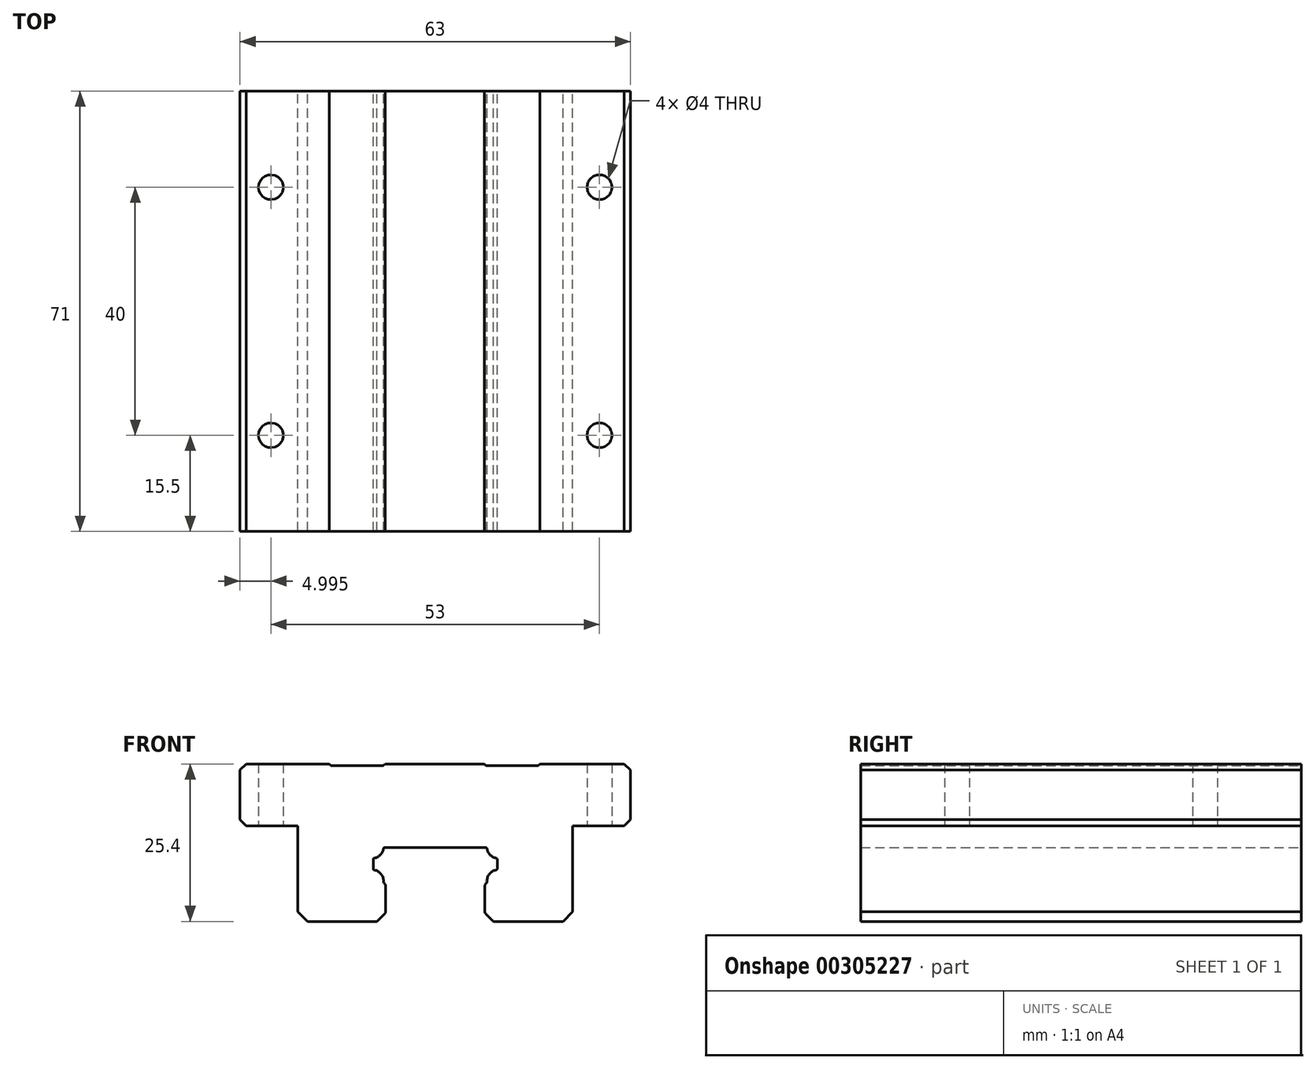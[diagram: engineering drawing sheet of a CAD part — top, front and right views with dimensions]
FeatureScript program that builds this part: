
annotation { "Feature Type Name" : "Feature", "Feature Type Description" : "" }
export const myFeature = defineFeature(function(context is Context, id is Id, definition is map)
    precondition{}
    {
        {
            var Q0;
            Q0=qCreatedBy(makeId("Front.planeOp"),FACE);
            var sketch = newSketch(context, id + "F0", { "sketchPlane" : qUnion([Q0])});
            skLineSegment(sketch, "E0.0.0", {"start": v(9.4, -11.6) * mm, "end": v(9.42, -11.62) * mm});
            skLineSegment(sketch, "E0.0.1", {"start": v(9.42, -11.62) * mm, "end": v(20.62, -11.62) * mm});
            skLineSegment(sketch, "E0.0.2", {"start": v(20.62, -11.62) * mm, "end": v(22.17, -10.07) * mm});
            skLineSegment(sketch, "E0.0.3", {"start": v(22.17, -10.07) * mm, "end": v(22.17, -7.4) * mm});
            skLineSegment(sketch, "E0.0.7", {"start": v(30.04, 3.78) * mm, "end": v(30.52, 3.78) * mm});
            skLineSegment(sketch, "E0.0.8", {"start": v(30.52, 3.78) * mm, "end": v(31.52, 4.78) * mm});
            skLineSegment(sketch, "E0.0.9", {"start": v(31.52, 4.78) * mm, "end": v(31.52, 12.78) * mm});
            skLineSegment(sketch, "E0.0.10", {"start": v(31.52, 12.78) * mm, "end": v(30.52, 13.78) * mm});
            skLineSegment(sketch, "E0.0.11", {"start": v(30.52, 13.78) * mm, "end": v(16.92, 13.78) * mm});
            skLineSegment(sketch, "E0.0.12", {"start": v(16.92, 13.78) * mm, "end": v(16.76, 13.63) * mm});
            skArc(sketch, "E0.0.13", {"start": v(16.76, 13.63) * mm, "mid": v(16.6, 13.52) * mm, "end": v(16.4, 13.48) * mm});
            skLineSegment(sketch, "E0.0.14", {"start": v(16.4, 13.48) * mm, "end": v(8.42, 13.48) * mm});
            skArc(sketch, "E0.0.15", {"start": v(8.42, 13.48) * mm, "mid": v(8.23, 13.52) * mm, "end": v(8.07, 13.63) * mm});
            skLineSegment(sketch, "E0.0.16", {"start": v(8.07, 13.63) * mm, "end": v(7.92, 13.78) * mm});
            skLineSegment(sketch, "E0.0.17", {"start": v(7.92, 13.78) * mm, "end": v(-8.08, 13.78) * mm});
            skLineSegment(sketch, "E0.0.18", {"start": v(-8.08, 13.78) * mm, "end": v(-8.24, 13.63) * mm});
            skArc(sketch, "E0.0.19", {"start": v(-8.24, 13.63) * mm, "mid": v(-8.4, 13.52) * mm, "end": v(-8.6, 13.48) * mm});
            skLineSegment(sketch, "E0.0.20", {"start": v(-8.6, 13.48) * mm, "end": v(-16.58, 13.48) * mm});
            skArc(sketch, "E0.0.21", {"start": v(-16.58, 13.48) * mm, "mid": v(-16.77, 13.52) * mm, "end": v(-16.93, 13.63) * mm});
            skLineSegment(sketch, "E0.0.22", {"start": v(-16.93, 13.63) * mm, "end": v(-17.08, 13.78) * mm});
            skLineSegment(sketch, "E0.0.23", {"start": v(-17.08, 13.78) * mm, "end": v(-30.48, 13.78) * mm});
            skLineSegment(sketch, "E0.0.24", {"start": v(-30.48, 13.78) * mm, "end": v(-31.48, 12.78) * mm});
            skLineSegment(sketch, "E0.0.25", {"start": v(-31.48, 12.78) * mm, "end": v(-31.48, 4.78) * mm});
            skLineSegment(sketch, "E0.0.26", {"start": v(-31.48, 4.78) * mm, "end": v(-30.48, 3.78) * mm});
            skLineSegment(sketch, "E0.0.27", {"start": v(-30.48, 3.78) * mm, "end": v(-30, 3.78) * mm});
            skLineSegment(sketch, "E0.0.31", {"start": v(-22.13, -7.4) * mm, "end": v(-22.13, -10.07) * mm});
            skLineSegment(sketch, "E0.0.32", {"start": v(-22.13, -10.07) * mm, "end": v(-20.58, -11.62) * mm});
            skLineSegment(sketch, "E0.0.33", {"start": v(-20.58, -11.62) * mm, "end": v(-9.38, -11.62) * mm});
            skLineSegment(sketch, "E0.0.34", {"start": v(-9.38, -11.62) * mm, "end": v(-9.37, -11.6) * mm});
            skLineSegment(sketch, "E0.0.35", {"start": v(-9.37, -11.6) * mm, "end": v(-19.73, -11.6) * mm});
            skLineSegment(sketch, "E0.0.43", {"start": v(19.77, -11.6) * mm, "end": v(9.4, -11.6) * mm});
            skLineSegment(sketch, "E1.0.0", {"start": v(8.16, -10.36) * mm, "end": v(9.4, -11.6) * mm});
            skLineSegment(sketch, "E1.0.1", {"start": v(9.4, -11.6) * mm, "end": v(19.77, -11.6) * mm});
            skLineSegment(sketch, "E1.0.9", {"start": v(-19.73, -11.6) * mm, "end": v(-9.37, -11.6) * mm});
            skLineSegment(sketch, "E1.0.10", {"start": v(-9.37, -11.6) * mm, "end": v(-8.13, -10.36) * mm});
            skArc(sketch, "E1.0.11", {"start": v(-8.13, -10.36) * mm, "mid": v(-8.02, -10.2) * mm, "end": v(-7.98, -10.01) * mm});
            skLineSegment(sketch, "E1.0.12", {"start": v(-7.98, -10.01) * mm, "end": v(-7.98, -5.93) * mm});
            skArc(sketch, "E1.0.13", {"start": v(-7.98, -5.93) * mm, "mid": v(-8.02, -5.73) * mm, "end": v(-8.13, -5.57) * mm});
            skLineSegment(sketch, "E1.0.14", {"start": v(-8.13, -5.57) * mm, "end": v(-8.27, -5.43) * mm});
            skArc(sketch, "E1.0.15", {"start": v(-8.27, -5.43) * mm, "mid": v(-8.32, -5.36) * mm, "end": v(-8.33, -5.27) * mm});
            skArc(sketch, "E1.0.16", {"start": v(-8.33, -5.27) * mm, "mid": v(-8.7, -4) * mm, "end": v(-9.82, -3.33) * mm});
            skArc(sketch, "E1.0.17", {"start": v(-9.82, -3.33) * mm, "mid": v(-9.94, -3.26) * mm, "end": v(-9.98, -3.13) * mm});
            skLineSegment(sketch, "E1.0.18", {"start": v(-9.98, -3.13) * mm, "end": v(-9.98, -1.6) * mm});
            skArc(sketch, "E1.0.19", {"start": v(-9.98, -1.6) * mm, "mid": v(-9.94, -1.47) * mm, "end": v(-9.82, -1.4) * mm});
            skArc(sketch, "E1.0.20", {"start": v(-9.82, -1.4) * mm, "mid": v(-8.83, -0.89) * mm, "end": v(-8.34, 0.11) * mm});
            skArc(sketch, "E1.0.21", {"start": v(-8.34, 0.11) * mm, "mid": v(-8.27, 0.23) * mm, "end": v(-8.14, 0.28) * mm});
            skLineSegment(sketch, "E1.0.22", {"start": v(-8.14, 0.28) * mm, "end": v(8.17, 0.28) * mm});
            skArc(sketch, "E1.0.23", {"start": v(8.17, 0.28) * mm, "mid": v(8.3, 0.23) * mm, "end": v(8.37, 0.11) * mm});
            skArc(sketch, "E1.0.24", {"start": v(8.37, 0.11) * mm, "mid": v(8.86, -0.89) * mm, "end": v(9.85, -1.4) * mm});
            skArc(sketch, "E1.0.25", {"start": v(9.85, -1.4) * mm, "mid": v(9.97, -1.47) * mm, "end": v(10.02, -1.6) * mm});
            skLineSegment(sketch, "E1.0.26", {"start": v(10.02, -1.6) * mm, "end": v(10.02, -3.13) * mm});
            skArc(sketch, "E1.0.27", {"start": v(10.02, -3.13) * mm, "mid": v(9.97, -3.26) * mm, "end": v(9.85, -3.33) * mm});
            skArc(sketch, "E1.0.28", {"start": v(9.85, -3.33) * mm, "mid": v(8.72, -4) * mm, "end": v(8.36, -5.27) * mm});
            skArc(sketch, "E1.0.29", {"start": v(8.36, -5.27) * mm, "mid": v(8.35, -5.36) * mm, "end": v(8.3, -5.43) * mm});
            skLineSegment(sketch, "E1.0.30", {"start": v(8.3, -5.43) * mm, "end": v(8.16, -5.57) * mm});
            skArc(sketch, "E1.0.31", {"start": v(8.16, -5.57) * mm, "mid": v(8.05, -5.73) * mm, "end": v(8.02, -5.93) * mm});
            skLineSegment(sketch, "E1.0.32", {"start": v(8.02, -5.93) * mm, "end": v(8.02, -10.01) * mm});
            skArc(sketch, "E1.0.33", {"start": v(8.02, -10.01) * mm, "mid": v(8.05, -10.2) * mm, "end": v(8.16, -10.36) * mm});
            skLineSegment(sketch, "E2", {"start": v(-30.48, 3.78) * mm, "end": v(-22.13, 3.78) * mm});
            skLineSegment(sketch, "E3", {"start": v(-22.13, 3.78) * mm, "end": v(-22.13, -7.4) * mm});
            skLineSegment(sketch, "E4", {"start": v(22.17, -7.4) * mm, "end": v(22.17, 3.78) * mm});
            skLineSegment(sketch, "E5", {"start": v(22.17, 3.78) * mm, "end": v(30.04, 3.78) * mm});
            skSolve(sketch);
        }
        {
            var Q0;
            Q0=makeQuery(id+"F0.imprint","IMPRINT",FACE,{"disambiguationData":[TD([[makeQuery(id+"F0.imprint","IMPRINT",EDGE,{"derivedFrom":sQuery(id+"F0.wireOp",EDGE,"E0.0.0")}),1.0]])]});
            extrude(context, id + "F1", {"entities" : qUnion([Q0]), "depth" : 71 * mm});
        }
        {
            var Q0;
            Q0=makeQuery(id+"F1.opExtrude","SWEPT_FACE",FACE,{"disambiguationData":[OSD([sQuery(id+"F0.wireOp",EDGE,"E1.0.22")])]});
            var sketch = newSketch(context, id + "F2", { "sketchPlane" : qUnion([Q0])});
            skLineSegment(sketch, "E6.0", {"start": v(-31.48, 71) * mm, "end": v(-31.48, 0) * mm});
            skLineSegment(sketch, "E7.0", {"start": v(31.52, 71) * mm, "end": v(31.52, 0) * mm});
            skLineSegment(sketch, "E8.0", {"start": v(0.02, 71) * mm, "end": v(0.02, 0) * mm});
            skPoint(sketch, "E9", {"position": v(-26.48, 55.5) * mm});
            skPoint(sketch, "E10", {"position": v(26.52, 55.5) * mm});
            skPoint(sketch, "E11", {"position": v(-26.48, 15.5) * mm});
            skPoint(sketch, "E12", {"position": v(26.52, 15.5) * mm});
            skSolve(sketch);
        }
        {
            var Q0;
            Q0=sQuery(id+"F2.wireOp",VERTEX,"E9");
            var Q1;
            Q1=sQuery(id+"F2.wireOp",VERTEX,"E10");
            var Q2;
            Q2=sQuery(id+"F2.wireOp",VERTEX,"E12");
            var Q3;
            Q3=sQuery(id+"F2.wireOp",VERTEX,"E11");
            var Q4;
            Q4=makeQuery(id+"F1.opExtrude","SWEPT_BODY",BODY,{"disambiguationData":[OSD([sQuery(id+"F0.wireOp",EDGE,"E0.0.0"),sQuery(id+"F0.wireOp",EDGE,"E0.0.1"),sQuery(id+"F0.wireOp",EDGE,"E0.0.2"),sQuery(id+"F0.wireOp",EDGE,"E0.0.3"),sQuery(id+"F0.wireOp",EDGE,"E0.0.7"),sQuery(id+"F0.wireOp",EDGE,"E0.0.8"),sQuery(id+"F0.wireOp",EDGE,"E0.0.9"),sQuery(id+"F0.wireOp",EDGE,"E0.0.10"),sQuery(id+"F0.wireOp",EDGE,"E0.0.11"),sQuery(id+"F0.wireOp",EDGE,"E0.0.12"),sQuery(id+"F0.wireOp",EDGE,"E0.0.13"),sQuery(id+"F0.wireOp",EDGE,"E0.0.14"),sQuery(id+"F0.wireOp",EDGE,"E0.0.15"),sQuery(id+"F0.wireOp",EDGE,"E0.0.16"),sQuery(id+"F0.wireOp",EDGE,"E0.0.17"),sQuery(id+"F0.wireOp",EDGE,"E0.0.18"),sQuery(id+"F0.wireOp",EDGE,"E0.0.19"),sQuery(id+"F0.wireOp",EDGE,"E0.0.20"),sQuery(id+"F0.wireOp",EDGE,"E0.0.21"),sQuery(id+"F0.wireOp",EDGE,"E0.0.22"),sQuery(id+"F0.wireOp",EDGE,"E0.0.23"),sQuery(id+"F0.wireOp",EDGE,"E0.0.24"),sQuery(id+"F0.wireOp",EDGE,"E0.0.25"),sQuery(id+"F0.wireOp",EDGE,"E0.0.26"),sQuery(id+"F0.wireOp",EDGE,"E0.0.31"),sQuery(id+"F0.wireOp",EDGE,"E0.0.32"),sQuery(id+"F0.wireOp",EDGE,"E0.0.33"),sQuery(id+"F0.wireOp",EDGE,"E0.0.34"),sQuery(id+"F0.wireOp",EDGE,"E1.0.0"),sQuery(id+"F0.wireOp",EDGE,"E1.0.10"),sQuery(id+"F0.wireOp",EDGE,"E1.0.11"),sQuery(id+"F0.wireOp",EDGE,"E1.0.12"),sQuery(id+"F0.wireOp",EDGE,"E1.0.13"),sQuery(id+"F0.wireOp",EDGE,"E1.0.14"),sQuery(id+"F0.wireOp",EDGE,"E1.0.15"),sQuery(id+"F0.wireOp",EDGE,"E1.0.16"),sQuery(id+"F0.wireOp",EDGE,"E1.0.17"),sQuery(id+"F0.wireOp",EDGE,"E1.0.18"),sQuery(id+"F0.wireOp",EDGE,"E1.0.19"),sQuery(id+"F0.wireOp",EDGE,"E1.0.20"),sQuery(id+"F0.wireOp",EDGE,"E1.0.21"),sQuery(id+"F0.wireOp",EDGE,"E1.0.22"),sQuery(id+"F0.wireOp",EDGE,"E1.0.23"),sQuery(id+"F0.wireOp",EDGE,"E1.0.24"),sQuery(id+"F0.wireOp",EDGE,"E1.0.25"),sQuery(id+"F0.wireOp",EDGE,"E1.0.26"),sQuery(id+"F0.wireOp",EDGE,"E1.0.27"),sQuery(id+"F0.wireOp",EDGE,"E1.0.28"),sQuery(id+"F0.wireOp",EDGE,"E1.0.29"),sQuery(id+"F0.wireOp",EDGE,"E1.0.30"),sQuery(id+"F0.wireOp",EDGE,"E1.0.31"),sQuery(id+"F0.wireOp",EDGE,"E1.0.32"),sQuery(id+"F0.wireOp",EDGE,"E1.0.33"),sQuery(id+"F0.wireOp",EDGE,"E2"),sQuery(id+"F0.wireOp",EDGE,"E3"),sQuery(id+"F0.wireOp",EDGE,"E4"),sQuery(id+"F0.wireOp",EDGE,"E5")])]});
            hole(context, id + "F3", {"style" : HoleStyle.SIMPLE, "endStyle" : HoleEndStyle.THROUGH, "holeDiameter" : 4 * mm, "tappedDepth" : 12 * mm, "tapClearance" : 3, "startFromSketch" : true, "locations" : qUnion([Q0, Q1, Q2, Q3]), "scope" : qUnion([Q4])});
        }
    });
